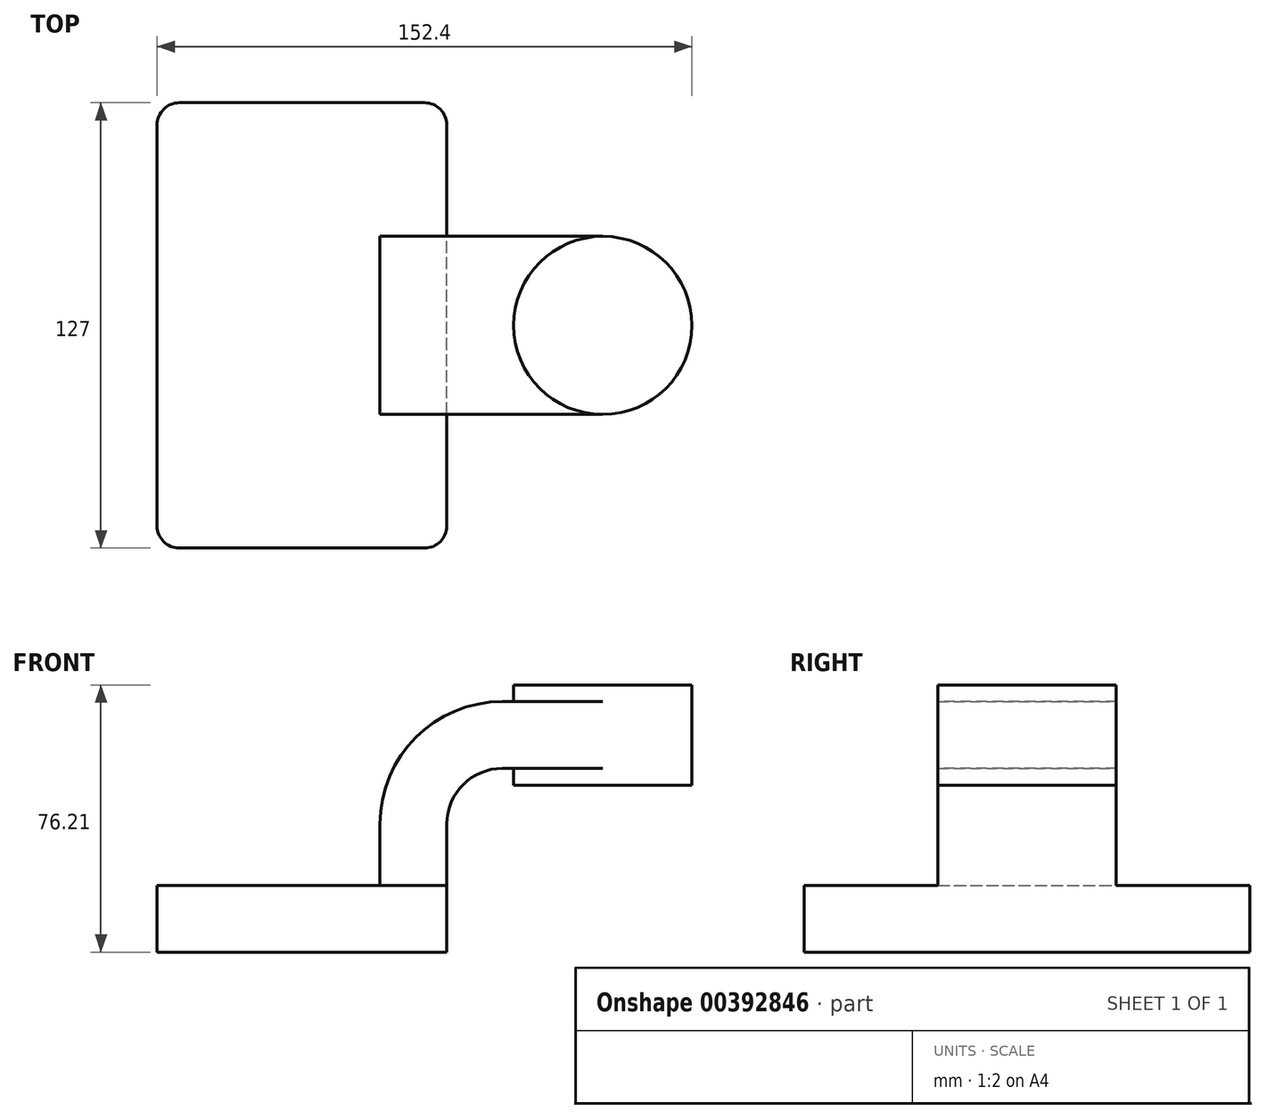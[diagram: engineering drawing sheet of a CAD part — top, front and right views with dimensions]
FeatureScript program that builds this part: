
annotation { "Feature Type Name" : "Feature", "Feature Type Description" : "" }
export const myFeature = defineFeature(function(context is Context, id is Id, definition is map)
    precondition{}
    {
        {
            var Q0;
            Q0=qCreatedBy(makeId("Front.planeOp"),FACE);
            var sketch = newSketch(context, id + "F0", { "sketchPlane" : qUnion([Q0])});
            skLineSegment(sketch, "E0.bottom", {"start": v(-41.28, 9.52) * mm, "end": v(41.27, 9.53) * mm});
            skLineSegment(sketch, "E0.top", {"start": v(-41.28, -9.53) * mm, "end": v(41.28, -9.53) * mm});
            skLineSegment(sketch, "E0.left", {"start": v(-41.28, 9.52) * mm, "end": v(-41.27, -9.53) * mm});
            skLineSegment(sketch, "E0.right", {"start": v(41.28, 9.53) * mm, "end": v(41.28, -9.52) * mm});
            skPoint(sketch, "E0.middle", {"position": v(0, 0) * mm});
            skLineSegment(sketch, "E1.bottom", {"start": v(60.33, 38.1) * mm, "end": v(111.13, 38.1) * mm});
            skLineSegment(sketch, "E1.top", {"start": v(60.33, 66.67) * mm, "end": v(111.13, 66.67) * mm});
            skLineSegment(sketch, "E1.left", {"start": v(60.33, 38.1) * mm, "end": v(60.33, 66.67) * mm});
            skLineSegment(sketch, "E1.right", {"start": v(111.13, 38.1) * mm, "end": v(111.13, 66.67) * mm});
            skPoint(sketch, "E1.middle", {"position": v(85.73, 52.39) * mm});
            skLineSegment(sketch, "E2", {"start": v(41.27, 9.53) * mm, "end": v(41.27, 27) * mm});
            skArc(sketch, "E3", {"start": v(41.27, 27) * mm, "mid": v(45.92, 38.23) * mm, "end": v(57.15, 42.88) * mm});
            skLineSegment(sketch, "E4", {"start": v(57.15, 42.88) * mm, "end": v(85.73, 42.88) * mm});
            skLineSegment(sketch, "E5.0", {"start": v(57.15, 61.93) * mm, "end": v(85.78, 61.93) * mm});
            skArc(sketch, "E5.1", {"start": v(22.23, 27) * mm, "mid": v(32.45, 51.7) * mm, "end": v(57.15, 61.93) * mm});
            skLineSegment(sketch, "E5.2", {"start": v(22.22, 9.53) * mm, "end": v(22.22, 27) * mm});
            skFitSpline(sketch, "E6", {"points": [v(-41.28, 9.52) * mm, v(57.15, 61.93) * mm], "startDerivative": vector(38.81, 114.57) * mm, "endDerivative": vector(171.45, -1.06) * mm});
            skLineSegment(sketch, "E7", {"start": v(85.72, 66.67) * mm, "end": v(85.72, 38.1) * mm});
            skSolve(sketch);
        }
        {
            var Q0;
            Q0=makeQuery(id+"F0.imprint","IMPRINT",FACE,{"disambiguationData":[TD([[makeQuery(id+"F0.imprint","IMPRINT",EDGE,{"derivedFrom":sQuery(id+"F0.wireOp",EDGE,"E0.top")}),1.0]])]});
            extrude(context, id + "F1", {"entities" : qUnion([Q0]), "depth" : 127 * mm, "symmetric" : true});
        }
        {
            var Q0;
            {var subQ5=sQuery(id+"F0.wireOp",EDGE,"8CDaNvw2-fq3g-PEdS-T8dk-5YbEPxcgNSmY");Q0=makeQuery(id+"F0.imprint","IMPRINT",FACE,{"disambiguationData":[TD([[makeQuery(id+"F0.imprint","IMPRINT",EDGE,{"derivedFrom":subQ5}),1.0]])]});}
            var Q1;
            {var subQ1=sQuery(id+"F0.wireOp",EDGE,"E2");Q1=makeQuery(id+"F0.imprint","IMPRINT",FACE,{"disambiguationData":[TD([[makeQuery(id+"F0.imprint","IMPRINT",EDGE,{"derivedFrom":subQ1}),1.0]])]});}
            extrude(context, id + "F2", {"entities" : qUnion([Q0, Q1]), "operationType" : NewBodyOperationType.ADD, "depth" : 50.8 * mm, "symmetric" : true});
        }
        {
            var Q0;
            Q0=makeQuery(id+"F0.imprint","IMPRINT",FACE,{"disambiguationData":[TD([[makeQuery(id+"F0.imprint","IMPRINT",EDGE,{"derivedFrom":sQuery(id+"F0.wireOp",EDGE,"E5.1")}),1.0]])]});
            extrude(context, id + "F3", {"entities" : qUnion([Q0]), "operationType" : NewBodyOperationType.ADD, "depth" : 15.88 * mm, "symmetric" : true});
        }
        {
            var Q0;
            {var subQ0=sQuery(id+"F0.wireOp",EDGE,"E4");var subQ1=sQuery(id+"F0.wireOp",EDGE,"E1.left");var subQ2=makeQuery(id+"F0.imprint","INTERSECT",VERTEX,{"derivedFrom":[subQ1,subQ0]});Q0=makeQuery(id+"F0.imprint","IMPRINT",FACE,{"disambiguationData":[TD([[makeQuery(id+"F0.imprint","IMPRINT",EDGE,{"disambiguationData":[TD([[subQ2,-1.0]])],"derivedFrom":subQ1}),-1.0]])]});}
            extrude(context, id + "F4", {"entities" : qUnion([Q0]), "operationType" : NewBodyOperationType.ADD, "depth" : 50.8 * mm, "symmetric" : true});
        }
        {
            var Q0;
            {var subQ4=sQuery(id+"F0.wireOp",EDGE,"E1.right");Q0=makeQuery(id+"F0.imprint","IMPRINT",FACE,{"disambiguationData":[TD([[makeQuery(id+"F0.imprint","IMPRINT",EDGE,{"derivedFrom":subQ4}),1.0]])]});}
            var Q1;
            Q1=sQuery(id+"F0.wireOp",EDGE,"E7");
            revolve(context, id + "F5", {"operationType" : NewBodyOperationType.ADD, "entities" : qUnion([Q0]), "axis" : qUnion([Q1]), "revolveType" : RevolveType.FULL});
        }
        {
            var Q0;
            Q0=makeQuery(id+"F1.opExtrude","CAP_EDGE",EDGE,{"disambiguationData":[OSD([sQuery(id+"F0.wireOp",EDGE,"E0.left")])],"isStart":false});
            var Q1;
            Q1=makeQuery(id+"F1.opExtrude","CAP_EDGE",EDGE,{"disambiguationData":[OSD([sQuery(id+"F0.wireOp",EDGE,"E0.right")])],"isStart":false});
            var Q2;
            Q2=makeQuery(id+"F1.opExtrude","CAP_EDGE",EDGE,{"disambiguationData":[OSD([sQuery(id+"F0.wireOp",EDGE,"E0.right")])],"isStart":true});
            var Q3;
            Q3=makeQuery(id+"F1.opExtrude","CAP_EDGE",EDGE,{"disambiguationData":[OSD([sQuery(id+"F0.wireOp",EDGE,"E0.left")])],"isStart":true});
            fillet(context, id + "F6", {"entities" : qUnion([Q0, Q1, Q2, Q3]), "radius" : 6.35 * mm, "tangentPropagation" : true, "allowEdgeOverflow" : false});
        }
    });
